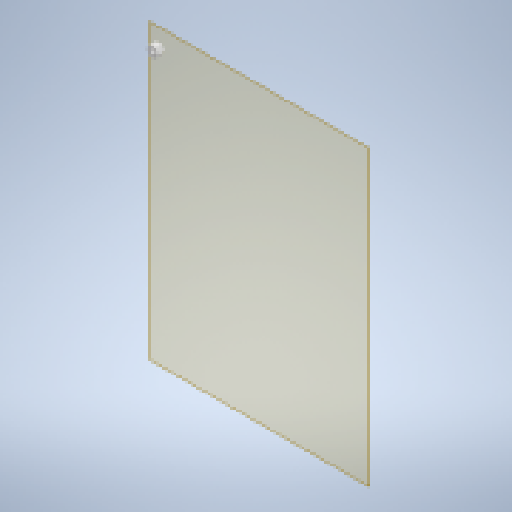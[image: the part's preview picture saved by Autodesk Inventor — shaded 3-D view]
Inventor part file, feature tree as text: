
AUTODESK INVENTOR PART (.ipt)
format: ipt  version: 2023 (Build 270158030, 158C)  size: 145,408 bytes
history: native  units: mm
features: other x3, plane x1, extrude x1, sketch x1
ambient origin geometry x8: Origin, YZ Plane, XZ Plane, XY Plane, X Axis, Y Axis, Z Axis, Center Point
bodies: Solid1 (feature_tree)
feature tree (6):
  plane  "Work Plane1"
  extrude  "Extrusion1"  Depth=11.85mm
  sketch  "Sketch1"  dims[d0=17.0mm d1=7.4mm d2=11.85mm d3=0.0mm]
  other  "<userpath>\Documents\0004-inventor\Inventor_Projects\electronics-enclosure\enclosure.iam"
  other  "enclosure.iam"
  other  "assembly-board:1"
